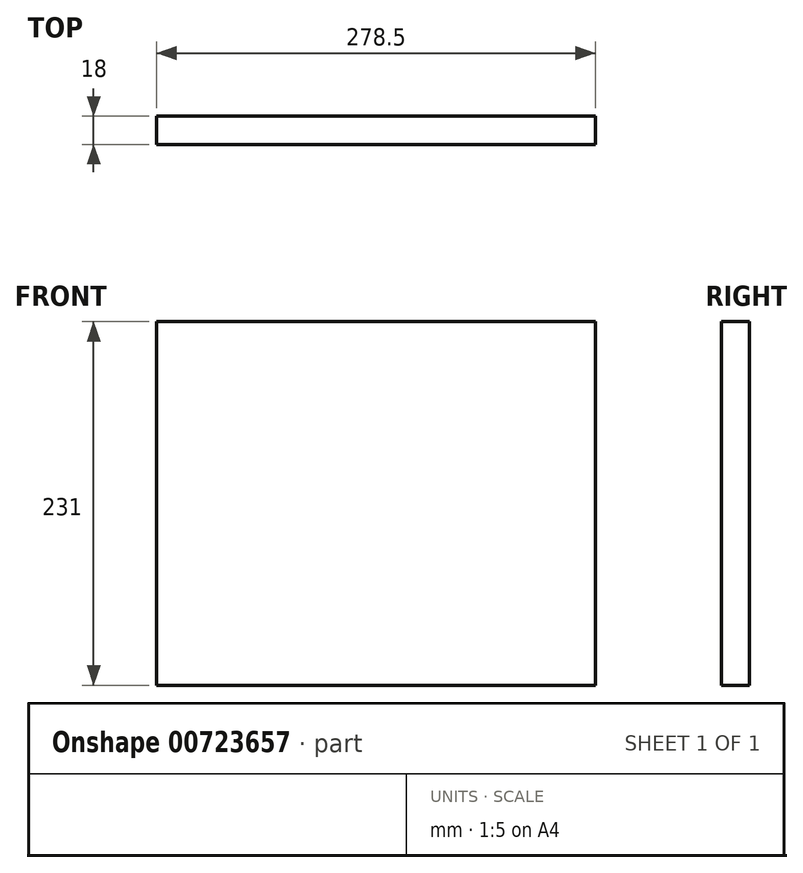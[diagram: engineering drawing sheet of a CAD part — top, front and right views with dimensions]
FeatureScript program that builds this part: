
annotation { "Feature Type Name" : "Feature", "Feature Type Description" : "" }
export const myFeature = defineFeature(function(context is Context, id is Id, definition is map)
    precondition{}
    {
        {
            var Q0;
            Q0=qCreatedBy(makeId("Front.planeOp"),FACE);
            var sketch = newSketch(context, id + "F0", { "sketchPlane" : qUnion([Q0])});
            skLineSegment(sketch, "E0.bottom", {"start": v(-139.25, 115.5) * mm, "end": v(139.25, 115.5) * mm});
            skLineSegment(sketch, "E0.top", {"start": v(-139.25, -115.5) * mm, "end": v(139.25, -115.5) * mm});
            skLineSegment(sketch, "E0.left", {"start": v(-139.25, 115.5) * mm, "end": v(-139.25, -115.5) * mm});
            skLineSegment(sketch, "E0.right", {"start": v(139.25, 115.5) * mm, "end": v(139.25, -115.5) * mm});
            skLineSegment(sketch, "E1", {"start": v(-139.25, 115.5) * mm, "end": v(139.25, -115.5) * mm, "construction": true});
            skLineSegment(sketch, "E2", {"start": v(139.25, 115.5) * mm, "end": v(-139.25, -115.5) * mm, "construction": true});
            skSolve(sketch);
        }
        {
            var Q0;
            Q0 = qSketchRegion(id + "F0", true);
            extrude(context, id + "F1", {"entities" : qUnion([Q0]), "depth" : 18 * mm, "offsetDistance" : 25 * mm});
        }
    });
